# Revit family: Clevertronics_CLIFE-RECSP
name_source: partatom
category: Lighting Fixtures
units: mm (PartAtom-declared; Revit-internal decimal feet)

## family parameters
Cut with Voids When Loaded = No
Host = Face
Light Source = Yes
Part Type = Normal
Room Calculation Point = No
Round Connector Dimension = Use Diameter
Shared = No

## types (9) — shared parameters
Apparent Load = 5 VA
Clevertronics_AS2293 Classification = C0=D50 C90=D50
Clevertronics_Applicable Standards = AS/NZS3820, CISPR15, AS/NZS2293.3
Clevertronics_Battery = 3.3V 3200mAh
Clevertronics_Battery Type = LLithium Iron Phosphate
Clevertronics_Ceiling Hole Cut-Out = 80mm
Clevertronics_Charger Method = Intelligent current limited constant voltage
Clevertronics_Construction = PC/ABS head
Clevertronics_Dimensions Main Enclosure = 232mm x 51mm x 42mm (Control pack)_95mm Head diameter
Clevertronics_Height = 42 mm  [stored 0.137795 ft]
Clevertronics_IP Rating = IP44 (parts below ceiling) IP20 (parts above ceiling)
Clevertronics_Length = 232 mm  [stored 0.761155 ft]
Clevertronics_Material = Clevertronics_Plycarbonate Base
Clevertronics_Minimum Ceiling Depth = 120mm
Clevertronics_Mounting = Recessed Ceiling
Clevertronics_Operating Mode = Non-maintained
Clevertronics_Operating Temperature = 1˚C to 40˚C
Clevertronics_Operating Voltage = 240V AC; 50Hz
Clevertronics_Replacement Battery = 1550010
Clevertronics_Width = 51 mm
Color Filter = 16777215
Default Elevation = 1200 mm
Dimming Lamp Color Temperature Shift = <None>
Lamp = Single LED (Lifetime warranty on the lamp head and loom assembly)
Manufacturer = Clevertronics
Photometric Web File = 200250PH(CLIFE-SM-WP-HV,AS2293.3,Photometry).ies
Tilt Angle = -90.00°
zero-valued in all types: Clevertronics_Annotation Size

## per-type parameters (varying)
| type | Clevertronics_Emergency Driver | Clevertronics_Emergency Lamp | Clevertronics_MIC Number | Clevertronics_Power Consumption | Clevertronics_Product Description | Clevertronics_Testing Node | Clevertronics_Testing System | Description | Model |
| CLIFE-RECSP_AUD02320030001 | AUM02370010001
LLIFE-CKIT
AUM01370030002
LLIFE-CKIT
AUM01370030002
LLIFE-CKIT
AUM01370030002 LLIFE-CKIT | 8050260 | AUD02320030001 | 1.0 Watts (Standby), 4.2 Watts (Max) | LP Premium Lifelight, High Performance, Recessed Emergency Light with IP44 Splash Proof Head, Enabled with Clevertest Plus |  | Clevertest Plus Enabled (Not activated by default) | LP Premium Lifelight, High Performance, Recessed Emergency Light with IP44 Splash Proof Head, Enabled with Clevertest Plus | CLIFE-RECSP |
| CLIFE-RECSP-BLK_AUD02320040001 | AUM02370010001
LLIFE-CKIT
AUM01370030002
LLIFE-CKIT
AUM01370030002
LLIFE-CKIT
AUM01370030002 LLIFE-CKIT | 8050250 | AUD02320040001 | 1.0 Watts (Standby), 4.2 Watts (Max) | LP Premium Lifelight, High Performance, Recessed Emergency Light with IP44 Splash Proof Head, Black, Enabled with Clevertest Plus |  | Clevertest Plus Enabled (Not activated by default) | LP Premium Lifelight, High Performance, Recessed Emergency Light with IP44 Splash Proof Head, Black, Enabled with Clevertest Plus | CLIFE-RECSP-BLK |
| CLIFE-RECSP-DALI_AUD02220030002 | AUM02270150102
LLIFE-CKIT
AUM01370030002
LLIFE-CKIT
AUM01370030002
LLIFE-CKIT
AUM01370030002 LLIFE-CKIT | 1100760 | AUD02220030002 | 1.3 Watts (Standby), 4.5 Watts (Max) | Lifelight IP44 Splashproof Emergency, Recessed Mount, LP, DALI Emergency, D50 | 8003060 | DALI Registered | Lifelight IP44 Splashproof Emergency, Recessed Mount, LP, DALI Emergency, D50 | CLIFE-RECSP-DALI |
| CLIFE-RECSP-DALI-BLK_AUD02210250002 | AUM02270150102
LLIFE-CKIT
AUM01370030002
LLIFE-CKIT
AUM01370030002
LLIFE-CKIT
AUM01370030002 LLIFE-CKIT | 1100762 | AUD02210250002 | 1.3 Watts (Standby), 4.5 Watts (Max) | LP Premium Lifelight, Recessed Emergency Light with IP44 Splash Proof Head, Black | 8003060 | DALI Registered | LP Premium Lifelight, Recessed Emergency Light with IP44 Splash Proof Head, Black | CLIFE-RECSP-DALI-BLK |
| CLIFE-RECSP-HV_AUD02820030001 | AUM02870080001
LLIFE-CKIT
AUM01370030002
LLIFE-CKIT
AUM01370030002
LLIFE-CKIT
AUM01370030002 LLIFE-CKIT | 1100760 | AUD02820030001 | 1.3 Watts (Standby), 4.5 Watts (Max) | Lifelight IP44 Splashproof Emergency, Recessed Mount, LP, Zoneworks XT Hive | 8003190 | Zoneworks XT HIVE (RF) | Lifelight IP44 Splashproof Emergency, Recessed Mount, LP, Zoneworks XT Hive | CLIFE-RECSP-HV |
| CLIFE-RECSP-HV-BLK_AUD02820090001 | AUM02870080001
LLIFE-CKIT
AUM01370030002
LLIFE-CKIT
AUM01370030002
LLIFE-CKIT
AUM01370030002 LLIFE-CKIT | 1100762 | AUD02820090001 | 1.3 Watts (Standby), 4.5 Watts (Max) | Lifelight IP44 Splashproof Emergency, Recessed Mount, LP, Zoneworks XT Hive, Black | 8003190 | Zoneworks XT HIVE (RF) | Lifelight IP44 Splashproof Emergency, Recessed Mount, LP, Zoneworks XT Hive, Black | CLIFE-RECSP-HV-BLK |
| CLIFE-RECSP-HV-TP_AUD02840020001 | AUM02870080001
LLIFE-CKIT
AUM01370030002
LLIFE-CKIT
AUM01370030002
LLIFE-CKIT
AUM01370030002 LLIFE-CKIT | 1100760 | AUD02840020001 | 1.3 Watts (Standby), 4.5 Watts (Max) | Lifelight IP44 Splashproof Emergency, Recessed Mount, LP, Zoneworks XT Hive, Tamperproof Screws, D50 | 8003191 | Zoneworks XT HIVE (RF) | Lifelight IP44 Splashproof Emergency, Recessed Mount, LP, Zoneworks XT Hive, Tamperproof Screws, D50 | CLIFE-RECSP-HV-TP |
| CLIFE-RECSP-HVG_AUD02920050001 | AUM02970020001
LLIFE-CKIT
AUM01370030002
LLIFE-CKIT
AUM01370030002
LLIFE-CKIT
AUM01370030002 LLIFE-CKIT | 1100760 | AUD02920050001 | 1.3 Watts (Standby), 4.5 Watts (Max) | Lifelight IP44 Splashproof Emergency, Recessed Mount, LP, Zoneworks XT Hive | 8003560 | Zoneworks XT HIVE (RF) 2.4GHz | Lifelight IP44 Splashproof Emergency, Recessed Mount, LP, Zoneworks XT Hive | CLIFE-RECSP-HVG |
| CLIFE-RECSP-ZW_AUD02120020001 | AUM02170120001
LLIFE-CKIT
AUM01370030002
LLIFE-CKIT
AUM01370030002
LLIFE-CKIT
AUM01370030002 LLIFE-CKIT | 1100760 | AUD02120020001 | 1.3 Watts (Standby), 4.5 Watts (Max) | Lifelight IP44 Splashproof Emergency, Recessed Mount, LP, Zoneworks XT | 8001450 | Zoneworks Computerised Testing | Lifelight IP44 Splashproof Emergency, Recessed Mount, LP, Zoneworks XT | CLIFE-RECSP-ZW |

note: [stored X ft] marks values corroborated as IEEE doubles in the binary element streams (Revit-internal decimal feet)

## geometry (parser evidence)
native form markers: Blend x4, Sweep x3
no freeform markers — native parametric forms only
